# Revit family: Haworth_Massimosistema_PeninsularModule_WithoutArms
name_source: partatom
category: Furniture
revit_build: Autodesk Revit 2018 (Build: 20170223_1515(x64)
units: mm (PartAtom-declared; Revit-internal decimal feet)

## family parameters
Always vertical = Yes
Cut with Voids When Loaded = No
OmniClass Number = 23.40.20.00
OmniClass Title = General Furniture and Specialties
Room Calculation Point = No
Shared = No
Work Plane-Based = No

## types (1)
- HCPF-MSPX
    Actual Depth = 55"
    Actual Height = 33 3/4"
    Actual Width = 50 1/2"
    Assembly Code = E2020200
    Back End = 50 1/2"
    Description = Haworth Massimosistema Sofa - Peninsular Module - Armless
    Frame Finish = Haworth _ Paint _ Metallic Gunmetal
    Manufacturer = Haworth
    Model = HCPF-MSPX
    Seat Depth = 34 3/4"
    Size = Verify Final Dim. w/ Haworth
    URL = http://www.haworth.com
    URL - Product = http://www.haworth.com
    Version = 1
    Warranty = https://www.haworth.com

## geometry (parser evidence)
native form markers: Sweep x10
no freeform markers — native parametric forms only
